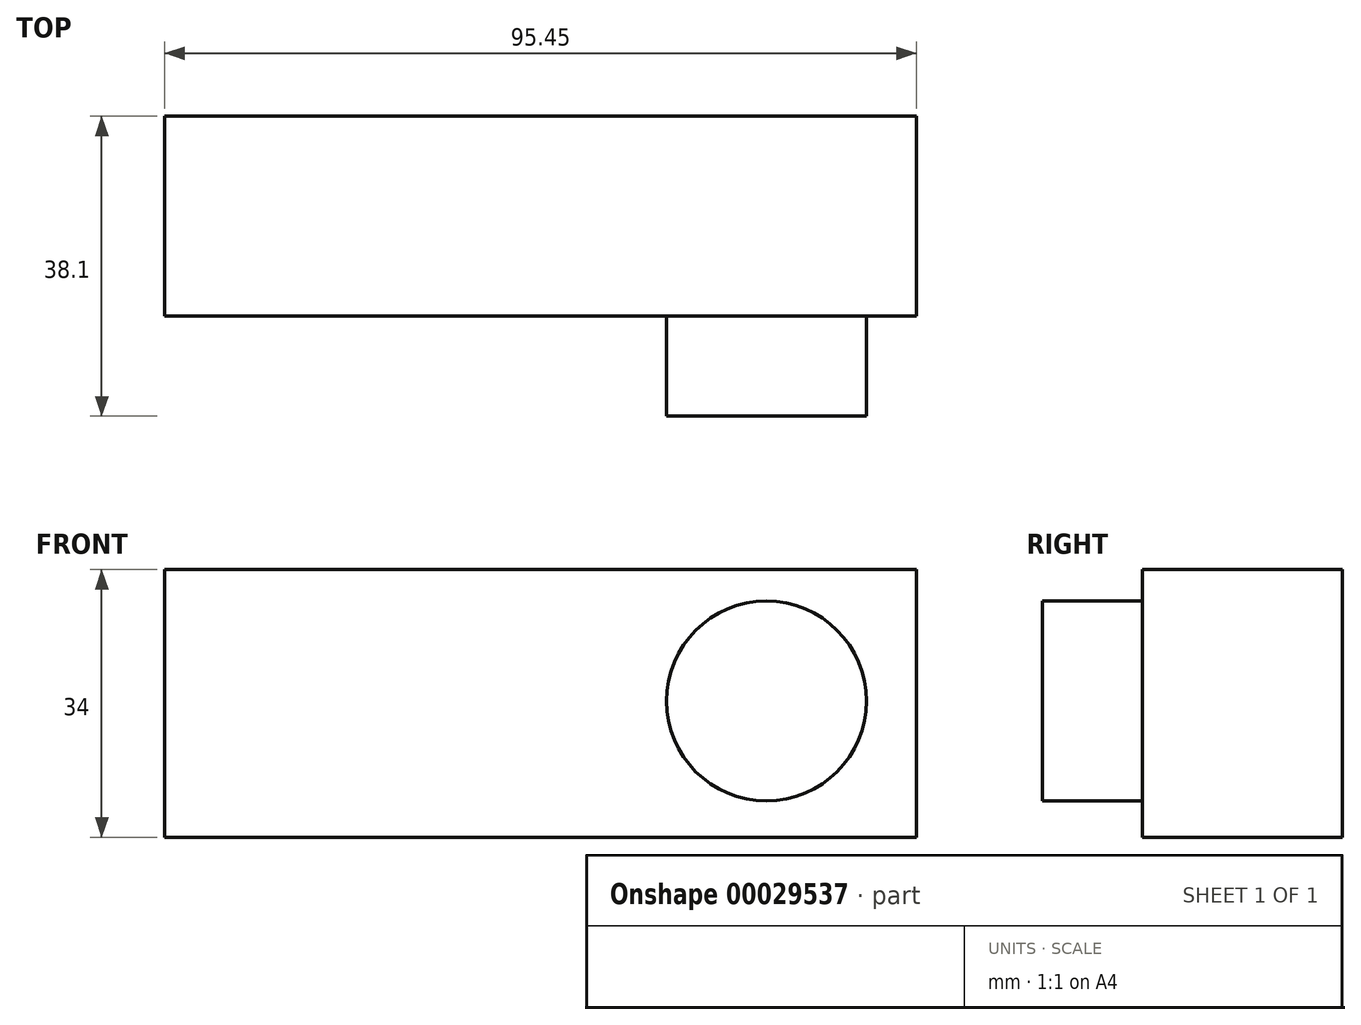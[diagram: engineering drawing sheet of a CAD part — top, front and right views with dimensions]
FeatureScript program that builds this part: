
annotation { "Feature Type Name" : "Feature", "Feature Type Description" : "" }
export const myFeature = defineFeature(function(context is Context, id is Id, definition is map)
    precondition{}
    {
        {
            var Q0;
            Q0=qCreatedBy(makeId("Front.planeOp"),FACE);
            var sketch = newSketch(context, id + "F0", { "sketchPlane" : qUnion([Q0])});
            skCircle(sketch, "E0", {"center": v(0, 0) * mm, "radius": 12.7 * mm});
            skLineSegment(sketch, "E1.rect.left", {"start": v(19.03, 16.69) * mm, "end": v(19.03, -17.31) * mm});
            skLineSegment(sketch, "E1.rect.right", {"start": v(-76.42, 16.69) * mm, "end": v(-76.42, -17.31) * mm});
            skPoint(sketch, "E1.rect.middle", {"position": v(-28.7, 0) * mm});
            skLineSegment(sketch, "E2", {"start": v(-76.42, 16.69) * mm, "end": v(19.03, 16.69) * mm});
            skLineSegment(sketch, "E3", {"start": v(0, -17.31) * mm, "end": v(19.03, -17.31) * mm});
            skLineSegment(sketch, "E4", {"start": v(0, -17.31) * mm, "end": v(-76.42, -17.31) * mm});
            skPoint(sketch, "E5.orphan", {"position": v(-76.42, 24.17) * mm});
            skPoint(sketch, "E6.orphan", {"position": v(19.03, 24.17) * mm});
            skPoint(sketch, "E1.rect.top.start.orphan", {"position": v(19.03, -24.17) * mm});
            skPoint(sketch, "E7.orphan", {"position": v(-76.42, -24.17) * mm});
            skSolve(sketch);
        }
        {
            var Q0;
            Q0=makeQuery(id+"F0.imprint","IMPRINT",FACE,{"disambiguationData":[TD([[makeQuery(id+"F0.imprint","IMPRINT",EDGE,{"derivedFrom":sQuery(id+"F0.wireOp",EDGE,"E0")}),1.0]])]});
            extrude(context, id + "F1", {"entities" : qUnion([Q0]), "depth" : 38.1 * mm});
        }
        {
            var Q0;
            Q0 = qSketchRegion(id + "F0", true);
            extrude(context, id + "F2", {"entities" : qUnion([Q0]), "operationType" : NewBodyOperationType.ADD, "depth" : 25.4 * mm});
        }
    });
